# Revit family: QF_ADVENTYS_MOP4I_16000_250902084646
name_source: partatom
category: Specialty Equipment
units: mm (PartAtom-declared; Revit-internal decimal feet)

## family parameters
Always vertical = Yes
Cut with Voids When Loaded = No
OmniClass Number = 23.40.40.14
OmniClass Title = Food Service Equipment
Part Type = Normal
Room Calculation Point = No
Round Connector Dimension = Use Diameter
Shared = No
Work Plane-Based = No

## types (1)
- ADV2048
    Accessory = No
    Cost = 0 $
    Default Elevation = 0 mm  [stored 0 ft]
    Depth Actual = 800 mm  [stored 2.62467 ft]
    Description = INDUCTION PLANCHA MODULE 4 ZONES THREE-PHASE
    Height Actual = 456 mm  [stored 1.49606 ft]
    Hot Water Consumption = 0.0 L/s
    Length Actual = 800 mm  [stored 2.62467 ft]
    Manufacturer = ADVENTYS
    Model = MOP4I 16000
    URL = www.adventys.com
    Weight = 100.00 kg

note: [stored X ft] marks values corroborated as IEEE doubles in the binary element streams (Revit-internal decimal feet)

## geometry (parser evidence)
native form markers: Sweep x7
no freeform markers — native parametric forms only
